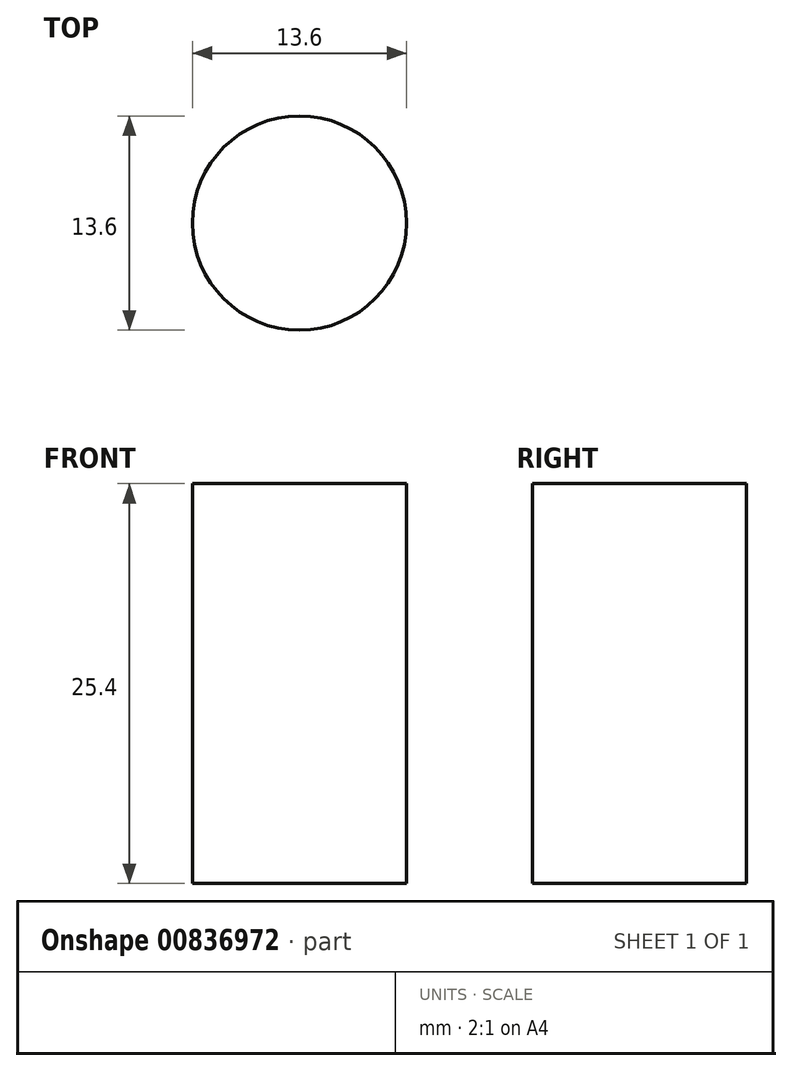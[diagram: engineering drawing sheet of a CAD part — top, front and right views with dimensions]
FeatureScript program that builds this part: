
annotation { "Feature Type Name" : "Feature", "Feature Type Description" : "" }
export const myFeature = defineFeature(function(context is Context, id is Id, definition is map)
    precondition{}
    {
        {
            var Q0;
            Q0=qCreatedBy(makeId("Top.planeOp"),FACE);
            var sketch = newSketch(context, id + "F0", { "sketchPlane" : qUnion([Q0])});
            skCircle(sketch, "E0", {"center": v(0, 0) * mm, "radius": 6.8 * mm});
            skSolve(sketch);
        }
        {
            var Q0;
            Q0=sQuery(id+"F0.wireOp",EDGE,"E0");
            extrude(context, id + "F1", {"bodyType" : ToolBodyType.SURFACE, "surfaceEntities" : qUnion([Q0]), "depth" : 25.4 * mm, "offsetDistance" : 25.4 * mm});
        }
    });
